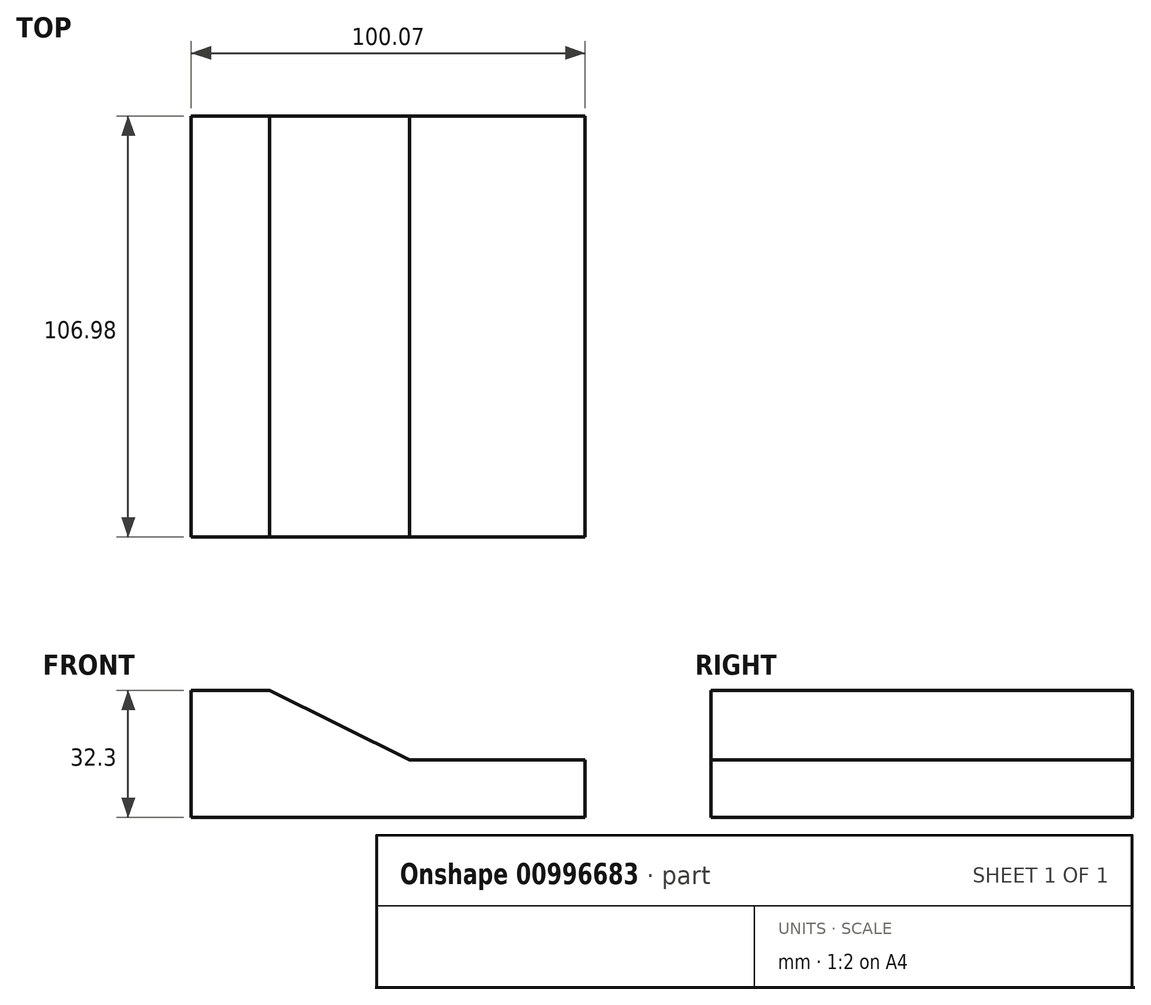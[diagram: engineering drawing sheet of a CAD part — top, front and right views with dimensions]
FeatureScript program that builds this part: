
annotation { "Feature Type Name" : "Feature", "Feature Type Description" : "" }
export const myFeature = defineFeature(function(context is Context, id is Id, definition is map)
    precondition{}
    {
        {
            var Q0;
            Q0=qCreatedBy(makeId("Front.planeOp"),FACE);
            var sketch = newSketch(context, id + "F0", { "sketchPlane" : qUnion([Q0])});
            skLineSegment(sketch, "E0", {"start": v(44.63, -41.98) * mm, "end": v(-55.44, -41.98) * mm});
            skLineSegment(sketch, "E1", {"start": v(-55.44, -41.98) * mm, "end": v(-55.44, -9.68) * mm});
            skLineSegment(sketch, "E2", {"start": v(-55.44, -9.68) * mm, "end": v(-35.58, -9.68) * mm});
            skLineSegment(sketch, "E3", {"start": v(-35.58, -9.68) * mm, "end": v(0, -27.31) * mm});
            skLineSegment(sketch, "E4", {"start": v(0, -27.31) * mm, "end": v(44.63, -27.31) * mm});
            skLineSegment(sketch, "E5", {"start": v(44.63, -27.31) * mm, "end": v(44.63, -41.98) * mm});
            skSolve(sketch);
        }
        {
            var Q0;
            Q0=makeQuery(id+"F0.imprint","IMPRINT",FACE,{"disambiguationData":[TD([[makeQuery(id+"F0.imprint","IMPRINT",EDGE,{"derivedFrom":sQuery(id+"F0.wireOp",EDGE,"E0")}),-1.0]])]});
            extrude(context, id + "F1", {"entities" : qUnion([Q0]), "oppositeDirection" : true, "depth" : 106.98 * mm, "offsetDistance" : 25.4 * mm});
        }
        {
            var Q0;
            Q0=makeQuery(id+"F1.opExtrude","SWEPT_BODY",BODY,{"disambiguationData":[OSD([sQuery(id+"F0.wireOp",EDGE,"E0"),sQuery(id+"F0.wireOp",EDGE,"E1"),sQuery(id+"F0.wireOp",EDGE,"E2"),sQuery(id+"F0.wireOp",EDGE,"E3"),sQuery(id+"F0.wireOp",EDGE,"E4"),sQuery(id+"F0.wireOp",EDGE,"E5")])]});
            transform(context, id + "F2", {"entities" : qUnion([Q0]), "transformType" : TransformType.TRANSLATION_3D, "dx" : 0 * mm, "dy" : -62.3 * mm, "dz" : 0 * mm, "makeCopy" : false});
        }
        {
            var Q0;
            Q0=makeQuery(id+"F1.opExtrude","SWEPT_FACE",FACE,{"disambiguationData":[OSD([sQuery(id+"F0.wireOp",EDGE,"E4")])]});
            var sketch = newSketch(context, id + "F3", { "sketchPlane" : qUnion([Q0])});
            skLineSegment(sketch, "E6", {"start": v(44.63, 24.54) * mm, "end": v(0, 24.54) * mm});
            skSolve(sketch);
        }
        {
            var Q0;
            Q0=qCreatedBy(makeId("Front.planeOp"),FACE);
            var Q1;
            Q1=sQuery(id+"F3.wireOp",VERTEX,"E6.end");
            cPlane(context, id + "F4", {"entities" : qUnion([Q0, Q1]), "cplaneType" : CPlaneType.PLANE_POINT, "offset" : 25.4 * mm, "width" : 152.4 * mm, "height" : 152.4 * mm});
        }
    });
